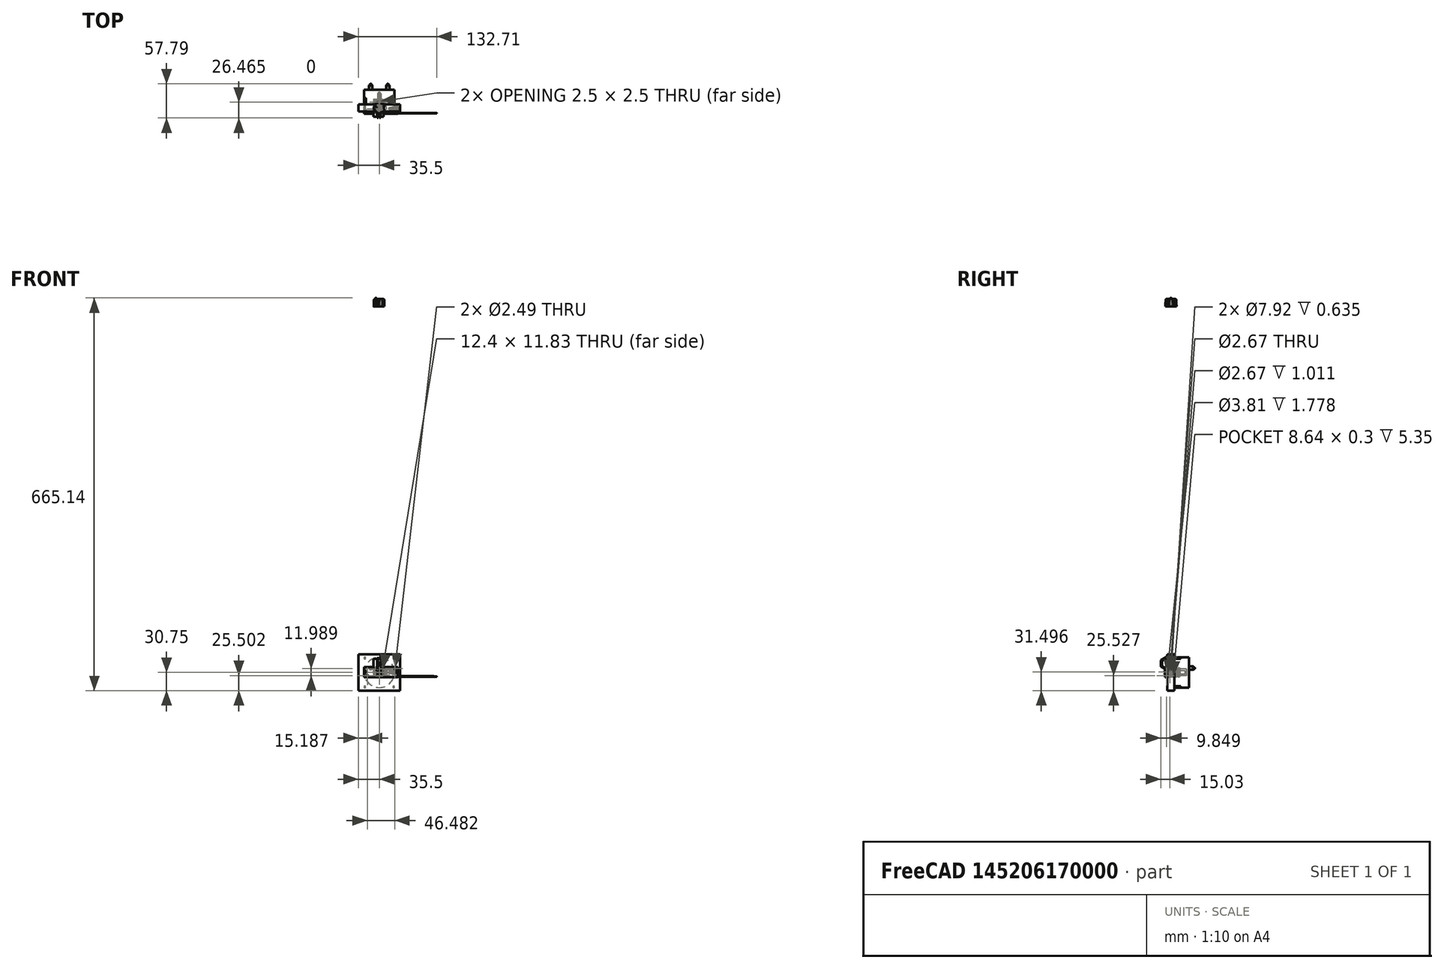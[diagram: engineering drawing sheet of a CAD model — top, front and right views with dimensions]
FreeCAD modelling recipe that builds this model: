
FCSTD DOCUMENT  (FreeCAD 1.0R39109 (Git))
Label: console-placement
License: All rights reserved
LicenseURL: https://en.wikipedia.org/wiki/All_rights_reserved
objects: App::Link×22, Part::Feature×7, App::FeaturePython×6, App::Part×3, Sketcher::SketchObject×3, PartDesign::Pad×3, Assembly::AssemblyLink×1, PartDesign::Plane×1, PartDesign::Body×1, Assembly::JointGroup×1, Assembly::AssemblyObject×1
note: 24 computed .brp shape members not serialized (recipe doc carries the construction recipe); baked Part::Feature solids carry a one-line shape summary decoded from their .brp
EXTERNAL_REF file=PCB.FCStd obj=Assembly
EXTERNAL_REF file=PCB.FCStd obj=pcb_imported
EXTERNAL_REF file=PCB.FCStd obj=WP154A4SUREQBFZGC
EXTERNAL_REF file=PCB.FCStd obj=WP154A4SUREQBFZGC001
EXTERNAL_REF file=PCB.FCStd obj=WP154A4SUREQBFZGC002
EXTERNAL_REF file=PCB.FCStd obj=WP154A4SUREQBFZGC003
EXTERNAL_REF file=PCB.FCStd obj=WP154A4SUREQBFZGC004
EXTERNAL_REF file=PCB.FCStd obj=WP154A4SUREQBFZGC005
EXTERNAL_REF file=PCB.FCStd obj=Dual_RCA
EXTERNAL_REF file=PCB.FCStd obj=Pro_Mini
EXTERNAL_REF file=PCB.FCStd obj=SPST_momentary001
EXTERNAL_REF file=PCB.FCStd obj=_pinconnector_640441_3
EXTERNAL_REF file=PCB.FCStd obj=_pinconnector_640441_004
EXTERNAL_REF file=PCB.FCStd obj=_pinconnector_640441_005
EXTERNAL_REF file=PCB.FCStd obj=CUI_PJ_202A
EXTERNAL_REF file=PCB.FCStd obj=SLW_864547_5A_RA_D
EXTERNAL_REF file=PCB.FCStd obj=SLW_864547_5A_RA_D001
EXTERNAL_REF file=PCB.FCStd obj=Ft232H_2_assembly001

FEATURE [App::Link] pcb_imported  label="pcb imported001"
  LinkedObject = -> <external PCB.FCStd>#pcb_imported
FEATURE [App::Link] WP154A4SUREQBFZGC  label="WP154A4SUREQBFZGC001"
  LinkPlacement = pos=(54.356,15.113,4.572) rot=(0,1,0;1.5708rad)
  LinkedObject = -> <external PCB.FCStd>#WP154A4SUREQBFZGC
  Placement = pos=(54.356,15.113,4.572) rot=(0,1,0;1.5708rad)
FEATURE [App::Link] WP154A4SUREQBFZGC001  label="WP154A4SUREQBFZGC002"
  LinkPlacement = pos=(54.356,28.448,4.572) rot=(0,1,0;1.5708rad)
  LinkedObject = -> <external PCB.FCStd>#WP154A4SUREQBFZGC001
  Placement = pos=(54.356,28.448,4.572) rot=(0,1,0;1.5708rad)
FEATURE [App::Link] WP154A4SUREQBFZGC002  label="WP154A4SUREQBFZGC003"
  LinkPlacement = pos=(54.356,50.038,4.572) rot=(0,1,0;1.5708rad)
  LinkedObject = -> <external PCB.FCStd>#WP154A4SUREQBFZGC002
  Placement = pos=(54.356,50.038,4.572) rot=(0,1,0;1.5708rad)
FEATURE [App::Link] WP154A4SUREQBFZGC003  label="WP154A4SUREQBFZGC004"
  LinkPlacement = pos=(54.356,63.373,4.572) rot=(0,1,0;1.5708rad)
  LinkedObject = -> <external PCB.FCStd>#WP154A4SUREQBFZGC003
  Placement = pos=(54.356,63.373,4.572) rot=(0,1,0;1.5708rad)
FEATURE [App::Link] WP154A4SUREQBFZGC004  label="WP154A4SUREQBFZGC005"
  LinkPlacement = pos=(54.356,84.963,4.572) rot=(0,1,0;1.5708rad)
  LinkedObject = -> <external PCB.FCStd>#WP154A4SUREQBFZGC004
  Placement = pos=(54.356,84.963,4.572) rot=(0,1,0;1.5708rad)
FEATURE [App::Link] WP154A4SUREQBFZGC005  label="WP154A4SUREQBFZGC006"
  LinkPlacement = pos=(54.356,98.298,4.572) rot=(0,1,0;1.5708rad)
  LinkedObject = -> <external PCB.FCStd>#WP154A4SUREQBFZGC005
  Placement = pos=(54.356,98.298,4.572) rot=(0,1,0;1.5708rad)
FEATURE [App::Link] Dual_RCA  label="Dual RCA001"
  LinkPlacement = pos=(0.032625,91.9586,15.028) rot=(0,0,-1;1.5708rad)
  LinkedObject = -> <external PCB.FCStd>#Dual_RCA
  Placement = pos=(0.032625,91.9586,15.028) rot=(0,0,-1;1.5708rad)
FEATURE [App::Link] Pro_Mini  label="Pro Mini001"
  LinkPlacement = pos=(28.575,39.37,11.938) rot=(0,0,1;4.71239rad)
  LinkedObject = -> <external PCB.FCStd>#Pro_Mini
  Placement = pos=(28.575,39.37,11.938) rot=(0,0,1;4.71239rad)
FEATURE [App::Link] SPST_momentary001  label="SPST-momentary001"
  LinkPlacement = pos=(9.02102,11.6417,1.678) rot=(-0.57735,0.57735,0.57735;4.18879rad)
  LinkedObject = -> <external PCB.FCStd>#SPST_momentary001
  Placement = pos=(9.02102,11.6417,1.678) rot=(-0.57735,0.57735,0.57735;4.18879rad)
FEATURE [App::Link] _pinconnector_640441_3  label="3pinconnector-640441-004"
  LinkPlacement = pos=(45.7412,2.54,1.778) rot=(0,1,0;3.14159rad)
  LinkedObject = -> <external PCB.FCStd>#_pinconnector_640441_3
  Placement = pos=(45.7412,2.54,1.778) rot=(0,1,0;3.14159rad)
FEATURE [App::Link] _pinconnector_640441_004  label="3pinconnector-640441-005"
  LinkPlacement = pos=(4.445,29.845,1.778) rot=(0,1,0;3.14159rad)
  LinkedObject = -> <external PCB.FCStd>#_pinconnector_640441_004
  Placement = pos=(4.445,29.845,1.778) rot=(0,1,0;3.14159rad)
FEATURE [App::Link] _pinconnector_640441_005  label="3pinconnector-640441-006"
  LinkPlacement = pos=(33.0962,92.7862,1.778) rot=(0,1,0;3.14159rad)
  LinkedObject = -> <external PCB.FCStd>#_pinconnector_640441_005
  Placement = pos=(33.0962,92.7862,1.778) rot=(0,1,0;3.14159rad)
FEATURE [App::Link] CUI_PJ_202A  label="CUI_PJ-202A001"
  LinkPlacement = pos=(-2.69501,66.04,8.278) rot=(0,0.707107,0.707107;3.14159rad)
  LinkedObject = -> <external PCB.FCStd>#CUI_PJ_202A
  Placement = pos=(-2.69501,66.04,8.278) rot=(0,0.707107,0.707107;3.14159rad)
FEATURE [App::Link] SLW_864547_5A_RA_D  label="SLW-864547-5A-RA-D001"
  LinkPlacement = pos=(2.563,37.056,1.72323) rot=(0,0,1;4.71239rad)
  LinkedObject = -> <external PCB.FCStd>#SLW_864547_5A_RA_D
  Placement = pos=(2.563,37.056,1.72323) rot=(0,0,1;4.71239rad)
FEATURE [App::Link] SLW_864547_5A_RA_D001  label="SLW-864547-5A-RA-D002"
  LinkPlacement = pos=(2.563,49.756,1.72323) rot=(0,0,1;4.71239rad)
  LinkedObject = -> <external PCB.FCStd>#SLW_864547_5A_RA_D001
  Placement = pos=(2.563,49.756,1.72323) rot=(0,0,1;4.71239rad)
FEATURE [App::Link] Ft232H_2_assembly001  label="Ft232H-2-assembly001"
  LinkPlacement = pos=(37.8726,15.185,11.684) rot=(1,0,0;1.5708rad)
  LinkedObject = -> <external PCB.FCStd>#Ft232H_2_assembly001
  Placement = pos=(37.8726,15.185,11.684) rot=(1,0,0;1.5708rad)
FEATURE [Assembly::AssemblyLink] PCB_Assembly  label="PCB Assembly"
  Group = -> [pcb_imported,WP154A4SUREQBFZGC,WP154A4SUREQBFZGC001,WP154A4SUREQBFZGC002,WP154A4SUREQBFZGC003,WP154A4SUREQBFZGC004,WP154A4SUREQBFZGC005,Dual_RCA,Pro_Mini,SPST_momentary001,_pinconnector_640441_3,_pinconnector_640441_004,_pinconnector_640441_005,CUI_PJ_202A,SLW_864547_5A_RA_D,SLW_864547_5A_RA_D001,Ft232H_2_assembly001]
  LinkedObject = -> <external PCB.FCStd>#Assembly
  Origin = -> Origin001
  Rigid = true
FEATURE [App::FeaturePython] GroundedJoint  # Assembly grounded joint (typed FeaturePython)
  ObjectToGround = -> PCB_Assembly
FEATURE [Part::Feature] Part__Feature  label="meter"
  shape: bbox 71 x 47.12 x 61.5 mm, 22 faces (baked)
FEATURE [App::Link] meter  label="meter001"
  LinkPlacement = pos=(82.55,12.7,55.88) rot=(0,0,1;1.5708rad)
  LinkedObject = -> Part__Feature
  Placement = pos=(82.55,12.7,55.88) rot=(0,0,1;1.5708rad)
FEATURE [App::FeaturePython] Joint  label="meter 1"  # Assembly joint (typed FeaturePython)
  Activated = true
  AngleMax = 0
  AngleMin = 0
  Detach1 = false
  Detach2 = false
  Distance = 0
  Distance2 = 0
  EnableAngleMax = false
  EnableAngleMin = false
  EnableLengthMax = false
  EnableLengthMin = false
  JointType = 0 (Fixed)
  LengthMax = 0
  LengthMin = 0
  Offset1 = pos=(-12.7,82.55,-55.88) rot=(0,0,-1;1.5708rad)
  Placement1 = pos=(-12.7,82.55,-55.88) rot=(0,0,-1;1.5708rad)
  Reference1 = -> Assembly [meter.,meter.]
  Reference2 = -> Assembly [PCB_Assembly.,PCB_Assembly.]
FEATURE [App::Link] meter001  label="meter002"
  LinkPlacement = pos=(82.55,101.6,55.88) rot=(0,0,1;1.5708rad)
  LinkedObject = -> Part__Feature
  Placement = pos=(82.55,101.6,55.88) rot=(0,0,1;1.5708rad)
FEATURE [App::FeaturePython] Joint001  label="meter 2 wrt 1"  # Assembly joint (typed FeaturePython)
  Activated = true
  AngleMax = 0
  AngleMin = 0
  Detach1 = false
  Detach2 = false
  Distance = 0
  Distance2 = 0
  EnableAngleMax = false
  EnableAngleMin = false
  EnableLengthMax = false
  EnableLengthMin = false
  JointType = 0 (Fixed)
  LengthMax = 0
  LengthMin = 0
  Offset1 = pos=(-88.9,0,0) rot=(0,0,1;0rad)
  Placement1 = pos=(-88.9,0,0) rot=(0,0,1;0rad)
  Reference1 = -> Assembly [meter001.,meter001.]
  Reference2 = -> Assembly [meter.,meter.]
FEATURE [Part::Feature] Part__Feature001  label="1M-pot"
  shape: bbox 24.75 x 24.5 x 16.5 mm, 34 faces (baked)
FEATURE [App::Link] _M_pot  label="1M-pot001"
  LinkPlacement = pos=(79.0499,-6.858,7.62) rot=(0.707107,0.707107,0;3.14159rad)
  LinkedObject = -> Part__Feature001
  Placement = pos=(79.0499,-6.858,7.62) rot=(0.707107,0.707107,0;3.14159rad)
FEATURE [App::FeaturePython] Joint002  label="pot joint"  # Assembly joint (typed FeaturePython)
  Activated = true
  AngleMax = 0
  AngleMin = 0
  Detach1 = false
  Detach2 = false
  Distance = 0
  Distance2 = 0
  EnableAngleMax = false
  EnableAngleMin = false
  EnableLengthMax = false
  EnableLengthMin = false
  JointType = 0 (Fixed)
  LengthMax = 0
  LengthMin = 0
  Offset1 = pos=(6.858,-79.0499,7.62) rot=(0,0,1;1.5708rad)
  Placement1 = pos=(6.858,-79.0499,7.62) rot=(0,0,1;1.5708rad)
  Reference1 = -> Assembly [_M_pot.,_M_pot.]
  Reference2 = -> Assembly [PCB_Assembly.,PCB_Assembly.]
FEATURE [Part::Feature] Part__Feature002  label="300DP6R7BLKM3QEBLK"
  shape: bbox 17.98 x 22.36 x 12.23 mm, 297 faces (baked)
FEATURE [Part::Feature] Part__Feature003  label="300DP6R7BLKM3QEBLK001"
  shape: bbox 19.85 x 2.3 x 15.8 mm, 12 faces (baked)
FEATURE [Part::Feature] Part__Feature004  label="300DP6R7BLKM3QEBLK002"
  shape: bbox 15.43 x 20.8 x 13 mm, 50 faces (baked)
FEATURE [App::Part] _00DP6R7BLKM3QEBLK  label="300DP6R7BLKM3QEBLK003"
  Group = -> [Part__Feature002,Part__Feature003,Part__Feature004]
  Origin = -> Origin002
FEATURE [App::Link] _00DP6R7BLKM3QEBLK003  label="300DP6R7BLKM3QEBLK004"
  LinkPlacement = pos=(77.7748,127,7.62) rot=(0.57735,0.57735,-0.57735;2.0944rad)
  LinkedObject = -> _00DP6R7BLKM3QEBLK
  Placement = pos=(77.7748,127,7.62) rot=(0.57735,0.57735,-0.57735;2.0944rad)
FEATURE [App::FeaturePython] Joint003  label="SP3T joint"  # Assembly joint (typed FeaturePython)
  Activated = true
  AngleMax = 0
  AngleMin = 0
  Detach1 = false
  Detach2 = false
  Distance = 0
  Distance2 = 0
  EnableAngleMax = false
  EnableAngleMin = false
  EnableLengthMax = false
  EnableLengthMin = false
  JointType = 0 (Fixed)
  LengthMax = 0
  LengthMin = 0
  Offset1 = pos=(7.62,-77.7748,127) rot=(0.57735,0.57735,0.57735;2.0944rad)
  Placement1 = pos=(7.62,-77.7748,127) rot=(0.57735,0.57735,0.57735;2.0944rad)
  Reference1 = -> Assembly [_00DP6R7BLKM3QEBLK003.,_00DP6R7BLKM3QEBLK003.]
  Reference2 = -> Assembly [PCB_Assembly.,PCB_Assembly.]
FEATURE [Sketcher::SketchObject] Sketch
  ArcFitTolerance = 1e-06
  AttachmentSupport = -> [XY_Plane004]
  FullyConstrained = true
  MakeInternals = false
  MapMode = 5
  sketch-geometry (1):
    g0: Circle CenterX=0 CenterY=0 CenterZ=0 NormalX=0 NormalY=0 NormalZ=1 AngleXU=0 Radius=9.15
  constraints (2):
    c: Coincident(g0,g-1)
    c: Diameter(g0) = 18.3
FEATURE [PartDesign::Pad] Pad
  Direction = (0,0,1)
  Length = 2
  Length2 = 10
  Profile = -> Sketch
  ReferenceAxis = -> Sketch [N_Axis]
  Refine = true
  Suppressed = false
  Type = 0
FEATURE [Sketcher::SketchObject] Sketch001
  ArcFitTolerance = 1e-06
  AttachmentSupport = -> [XY_Plane004]
  FullyConstrained = true
  MakeInternals = false
  MapMode = 5
  sketch-geometry (1):
    g0: Circle CenterX=0 CenterY=0 CenterZ=0 NormalX=0 NormalY=0 NormalZ=1 AngleXU=0 Radius=7.75
  constraints (2):
    c: Diameter(g0) = 15.5
    c: Coincident(g0,g-1)
FEATURE [PartDesign::Pad] Pad001
  BaseFeature = -> Pad
  Direction = (0,0,1)
  Length = 17
  Length2 = 10
  Midplane = true
  Profile = -> Sketch001
  ReferenceAxis = -> Sketch001 [N_Axis]
  Refine = true
  Suppressed = false
  Type = 0
FEATURE [PartDesign::Plane] DatumPlane
  AttachmentOffset = pos=(0,0,-2) rot=(0,0,1;0rad)
  AttachmentSupport = -> [XY_Plane004]
  Length = 60.0456
  MapMode = 5
  Placement = pos=(0,0,-2) rot=(0,0,1;0rad)
  ResizeMode = 0
  Width = 60.0456
FEATURE [Sketcher::SketchObject] Sketch002
  ArcFitTolerance = 1e-06
  AttachmentSupport = -> [DatumPlane]
  FullyConstrained = true
  MakeInternals = false
  MapMode = 5
  Placement = pos=(0,0,-2) rot=(0,0,1;0rad)
  sketch-geometry (7):
    g0: LineSegment StartX=-5.48483 StartY=9.5 StartZ=0 EndX=-10.9697 EndY=0 EndZ=0
    g1: LineSegment StartX=-10.9697 StartY=0 StartZ=0 EndX=-5.48483 EndY=-9.5 EndZ=0
    g2: LineSegment StartX=-5.48483 StartY=-9.5 StartZ=0 EndX=5.48483 EndY=-9.5 EndZ=0
    g3: LineSegment StartX=5.48483 StartY=-9.5 StartZ=0 EndX=10.9697 EndY=1.8e-15 EndZ=0
    g4: LineSegment StartX=10.9697 StartY=1.8e-15 StartZ=0 EndX=5.48483 EndY=9.5 EndZ=0
    g5: LineSegment StartX=5.48483 StartY=9.5 StartZ=0 EndX=-5.48483 EndY=9.5 EndZ=0
    g6: Circle [constr] CenterX=0 CenterY=0 CenterZ=0 NormalX=0 NormalY=0 NormalZ=1 AngleXU=0 Radius=10.9697
  constraints (16):
    c: Coincident(g0,g1)
    c: Coincident(g1,g2)
    c: Coincident(g2,g3)
    c: Coincident(g3,g4)
    c: Coincident(g4,g5)
    c: Coincident(g5,g0)
    c: Equal(g0, g1-g5) x5
    c: PointOnObject(g0,g6)
    c: PointOnObject(g1,g6)
    c: PointOnObject(g2,g6)
    c: PointOnObject(g3,g6)
    c: PointOnObject(g4,g6)
    c: PointOnObject(g5,g6)
    c: Coincident(g6,g-1)
    c: Horizontal(g5)
    c: DistanceY(g2,g4) = 19
FEATURE [PartDesign::Pad] Pad002
  BaseFeature = -> Pad001
  Direction = (0,0,1)
  Length = 2
  Length2 = 10
  Profile = -> Sketch002
  ReferenceAxis = -> Sketch002 [N_Axis]
  Refine = true
  Reversed = true
  Suppressed = false
  Type = 0
FEATURE [PartDesign::Body] Body
  AllowCompound = false
  Group = -> [Sketch,Pad,Sketch001,Pad001,DatumPlane,Sketch002,Pad002]
  Origin = -> Origin004
  Placement = pos=(-1.524,-7.62,15.24) rot=(0,1,0;4.71239rad)
  Tip = -> Pad002
FEATURE [App::Part] Part  label="Cliff FC684204"
  Group = -> [Body]
  Origin = -> Origin003
FEATURE [Part::Feature] Part__Feature005  label="AA single"
  shape: bbox 122.8 x 13.91 x 16.91 mm, 627 faces (baked)
FEATURE [App::Part] AA_single  label="AA single002"
  Group = -> [Part__Feature005]
  Origin = -> Origin005
FEATURE [Part::Feature] Part__Feature006  label="knob"
  shape: bbox 18.73 x 19.3 x 14.61 mm, 41 faces (baked)
FEATURE [App::Link] knob  label="knob001"
  LinkPlacement = pos=(-525.356,-6.858,7.62) rot=(0,1,0;1.5708rad)
  LinkedObject = -> Part__Feature006
  Placement = pos=(-525.356,-6.858,7.62) rot=(0,1,0;1.5708rad)
FEATURE [App::FeaturePython] Joint006  label="Revolute"  # Assembly joint (typed FeaturePython)
  Activated = true
  AngleMax = 0
  AngleMin = 0
  Detach1 = false
  Detach2 = false
  Distance = 0
  Distance2 = 0
  EnableAngleMax = false
  EnableAngleMin = false
  EnableLengthMax = false
  EnableLengthMin = false
  JointType = 1 (Revolute)
  LengthMax = 0
  LengthMin = 0
  Offset1 = pos=(0,0,203.2) rot=(0,0,1;0rad)
  Placement1 = pos=(-1.31779e-06,0,628.906) rot=(0,-1,0;3.14159rad)
  Placement2 = pos=(0,24.5,9e-16) rot=(-0.57735,-0.57735,0.57735;4.18879rad)
  Reference1 = -> Assembly [knob.Face2,knob.Face2]
  Reference2 = -> Assembly [_M_pot.Face6,_M_pot.Edge1]
FEATURE [Assembly::JointGroup] Joints
  Group = -> [GroundedJoint,Joint,Joint001,Joint002,Joint003,Joint006]
FEATURE [Assembly::AssemblyObject] Assembly
  Group = -> [Joints,PCB_Assembly,GroundedJoint,meter,Joint,meter001,Joint001,_M_pot,Joint002,_00DP6R7BLKM3QEBLK003,Joint003,knob,Joint006]
  Origin = -> Origin
  Type = Assembly

RESOLVED EXTERNAL PARTS (link-assembly join: the EXTERNAL_REF files above that resolve inside this repo's crawl, each included once):
---- part PCB.FCStd = doc fcstd_af2e7ee1fe31 ----
FCSTD DOCUMENT  (FreeCAD 1.0R39109 (Git))
Label: PCB
License: All rights reserved
LicenseURL: https://en.wikipedia.org/wiki/All_rights_reserved
objects: App::Link×17, App::FeaturePython×17, Part::Feature×15, Sketcher::SketchObject×3, App::Part×3, PartDesign::Pad×2, PartDesign::Body×2, PartDesign::Pocket×1, Assembly::JointGroup×1, Assembly::AssemblyObject×1, PartDesign::SubShapeBinder×1
note: 33 computed .brp shape members not serialized (recipe doc carries the construction recipe); baked Part::Feature solids carry a one-line shape summary decoded from their .brp

FEATURE [Sketcher::SketchObject] MainSketch
  ArcFitTolerance = 1e-06
  AttachmentSupport = -> [XY_Plane]
  FullyConstrained = false
  MakeInternals = false
  MapMode = 5
  sketch-geometry (4):
    g0: LineSegment StartX=0 StartY=0 StartZ=0 EndX=50.8 EndY=0 EndZ=0
    g1: LineSegment StartX=50.8 StartY=0 StartZ=0 EndX=50.8 EndY=101.6 EndZ=0
    g2: LineSegment StartX=50.8 StartY=101.6 StartZ=0 EndX=0 EndY=101.6 EndZ=0
    g3: LineSegment StartX=0 StartY=101.6 StartZ=0 EndX=0 EndY=0 EndZ=0
  constraints (4):
    c: Horizontal(g0)
    c: Horizontal(g2)
    c: Vertical(g1)
    c: Vertical(g3)
FEATURE [PartDesign::Pad] Main
  Direction = (0,0,1)
  Length = 1.778
  Length2 = 100.076
  Profile = -> MainSketch
  Refine = true
  Suppressed = false
  Type = 0
FEATURE [Sketcher::SketchObject] HoleSketch
  ArcFitTolerance = 1e-06
  AttachmentSupport = -> [XY_Plane]
  FullyConstrained = false
  MakeInternals = false
  MapMode = 5
  sketch-geometry (197):
    g0: Circle CenterX=41.275 CenterY=47.117 CenterZ=0 NormalX=0 NormalY=0 NormalZ=1 AngleXU=0 Radius=0.508
    g1: Circle CenterX=38.735 CenterY=47.117 CenterZ=0 NormalX=0 NormalY=0 NormalZ=1 AngleXU=0 Radius=0.508
    g2: Circle CenterX=36.195 CenterY=47.117 CenterZ=0 NormalX=0 NormalY=0 NormalZ=1 AngleXU=0 Radius=0.508
    g3: Circle CenterX=13.335 CenterY=47.117 CenterZ=0 NormalX=0 NormalY=0 NormalZ=1 AngleXU=0 Radius=0.508
    g4: Circle CenterX=33.655 CenterY=47.117 CenterZ=0 NormalX=0 NormalY=0 NormalZ=1 AngleXU=0 Radius=0.508
    g5: Circle CenterX=15.875 CenterY=47.117 CenterZ=0 NormalX=0 NormalY=0 NormalZ=1 AngleXU=0 Radius=0.508
    g6: Circle CenterX=31.115 CenterY=47.117 CenterZ=0 NormalX=0 NormalY=0 NormalZ=1 AngleXU=0 Radius=0.508
    g7: Circle CenterX=28.575 CenterY=47.117 CenterZ=0 NormalX=0 NormalY=0 NormalZ=1 AngleXU=0 Radius=0.508
    g8: Circle CenterX=26.035 CenterY=47.117 CenterZ=0 NormalX=0 NormalY=0 NormalZ=1 AngleXU=0 Radius=0.508
    g9: Circle CenterX=18.415 CenterY=47.117 CenterZ=0 NormalX=0 NormalY=0 NormalZ=1 AngleXU=0 Radius=0.508
    g10: Circle CenterX=20.955 CenterY=47.117 CenterZ=0 NormalX=0 NormalY=0 NormalZ=1 AngleXU=0 Radius=0.508
    g11: Circle CenterX=23.495 CenterY=47.117 CenterZ=0 NormalX=0 NormalY=0 NormalZ=1 AngleXU=0 Radius=0.508
    g12: Circle CenterX=15.875 CenterY=31.877 CenterZ=0 NormalX=0 NormalY=0 NormalZ=1 AngleXU=0 Radius=0.508
    g13: Circle CenterX=13.335 CenterY=31.877 CenterZ=0 NormalX=0 NormalY=0 NormalZ=1 AngleXU=0 Radius=0.508
    g14: Circle CenterX=20.955 CenterY=31.877 CenterZ=0 NormalX=0 NormalY=0 NormalZ=1 AngleXU=0 Radius=0.508
    g15: Circle CenterX=18.415 CenterY=31.877 CenterZ=0 NormalX=0 NormalY=0 NormalZ=1 AngleXU=0 Radius=0.508
    g16: Circle CenterX=26.035 CenterY=31.877 CenterZ=0 NormalX=0 NormalY=0 NormalZ=1 AngleXU=0 Radius=0.508
    g17: Circle CenterX=23.495 CenterY=31.877 CenterZ=0 NormalX=0 NormalY=0 NormalZ=1 AngleXU=0 Radius=0.508
    g18: Circle CenterX=31.115 CenterY=31.877 CenterZ=0 NormalX=0 NormalY=0 NormalZ=1 AngleXU=0 Radius=0.508
    g19: Circle CenterX=28.575 CenterY=31.877 CenterZ=0 NormalX=0 NormalY=0 NormalZ=1 AngleXU=0 Radius=0.508
    g20: Circle CenterX=36.195 CenterY=31.877 CenterZ=0 NormalX=0 NormalY=0 NormalZ=1 AngleXU=0 Radius=0.508
    g21: Circle CenterX=33.655 CenterY=31.877 CenterZ=0 NormalX=0 NormalY=0 NormalZ=1 AngleXU=0 Radius=0.508
    g22: Circle CenterX=41.275 CenterY=31.877 CenterZ=0 NormalX=0 NormalY=0 NormalZ=1 AngleXU=0 Radius=0.508
    g23: Circle CenterX=38.735 CenterY=31.877 CenterZ=0 NormalX=0 NormalY=0 NormalZ=1 AngleXU=0 Radius=0.508
    g24: Circle CenterX=22.225 CenterY=34.925 CenterZ=0 NormalX=0 NormalY=0 NormalZ=1 AngleXU=0 Radius=0.508
    g25: Circle CenterX=19.685 CenterY=34.925 CenterZ=0 NormalX=0 NormalY=0 NormalZ=1 AngleXU=0 Radius=0.508
    g26: Circle CenterX=32.385 CenterY=34.925 CenterZ=0 NormalX=0 NormalY=0 NormalZ=1 AngleXU=0 Radius=0.508
    g27: Circle CenterX=29.845 CenterY=34.925 CenterZ=0 NormalX=0 NormalY=0 NormalZ=1 AngleXU=0 Radius=0.508
    g28: Circle CenterX=43.815 CenterY=43.307 CenterZ=0 NormalX=0 NormalY=0 NormalZ=1 AngleXU=0 Radius=0.508
    g29: Circle CenterX=43.815 CenterY=40.767 CenterZ=0 NormalX=0 NormalY=0 NormalZ=1 AngleXU=0 Radius=0.508
    g30: Circle CenterX=43.815 CenterY=38.227 CenterZ=0 NormalX=0 NormalY=0 NormalZ=1 AngleXU=0 Radius=0.508
    g31: Circle CenterX=43.815 CenterY=35.687 CenterZ=0 NormalX=0 NormalY=0 NormalZ=1 AngleXU=0 Radius=0.508
    g32: Circle CenterX=43.815 CenterY=33.147 CenterZ=0 NormalX=0 NormalY=0 NormalZ=1 AngleXU=0 Radius=0.508
    g33: Circle CenterX=16.51 CenterY=25.4 CenterZ=0 NormalX=0 NormalY=0 NormalZ=1 AngleXU=0 Radius=0.508
    g34: Circle CenterX=8.89 CenterY=5.08 CenterZ=0 NormalX=0 NormalY=0 NormalZ=1 AngleXU=0 Radius=0.508
    g35: Circle CenterX=19.05 CenterY=25.4 CenterZ=0 NormalX=0 NormalY=0 NormalZ=1 AngleXU=0 Radius=0.508
    g36: Circle CenterX=11.43 CenterY=5.08 CenterZ=0 NormalX=0 NormalY=0 NormalZ=1 AngleXU=0 Radius=0.508
    g37: Circle CenterX=13.97 CenterY=5.08 CenterZ=0 NormalX=0 NormalY=0 NormalZ=1 AngleXU=0 Radius=0.508
    g38: Circle CenterX=16.51 CenterY=5.08 CenterZ=0 NormalX=0 NormalY=0 NormalZ=1 AngleXU=0 Radius=0.508
    g39: Circle CenterX=19.05 CenterY=5.08 CenterZ=0 NormalX=0 NormalY=0 NormalZ=1 AngleXU=0 Radius=0.508
    g40: Circle CenterX=21.59 CenterY=5.08 CenterZ=0 NormalX=0 NormalY=0 NormalZ=1 AngleXU=0 Radius=0.508
    g41: Circle CenterX=24.13 CenterY=5.08 CenterZ=0 NormalX=0 NormalY=0 NormalZ=1 AngleXU=0 Radius=0.508
    g42: Circle CenterX=26.67 CenterY=5.08 CenterZ=0 NormalX=0 NormalY=0 NormalZ=1 AngleXU=0 Radius=0.508
    g43: Circle CenterX=29.21 CenterY=25.4 CenterZ=0 NormalX=0 NormalY=0 NormalZ=1 AngleXU=0 Radius=0.508
    g44: Circle CenterX=29.21 CenterY=5.08 CenterZ=0 NormalX=0 NormalY=0 NormalZ=1 AngleXU=0 Radius=0.508
    g45: Circle CenterX=31.75 CenterY=25.4 CenterZ=0 NormalX=0 NormalY=0 NormalZ=1 AngleXU=0 Radius=0.508
    g46: Circle CenterX=31.75 CenterY=5.08 CenterZ=0 NormalX=0 NormalY=0 NormalZ=1 AngleXU=0 Radius=0.508
    g47: Circle CenterX=11.5358 CenterY=9.05933 CenterZ=0 NormalX=0 NormalY=0 NormalZ=1 AngleXU=0 Radius=0.508
    g48: Circle CenterX=11.5358 CenterY=14.1393 CenterZ=0 NormalX=0 NormalY=0 NormalZ=1 AngleXU=0 Radius=0.508
    g49: Circle CenterX=6.45583 CenterY=9.05933 CenterZ=0 NormalX=0 NormalY=0 NormalZ=1 AngleXU=0 Radius=0.508
    g50: Circle CenterX=6.45583 CenterY=14.1393 CenterZ=0 NormalX=0 NormalY=0 NormalZ=1 AngleXU=0 Radius=0.508
    g51: Circle CenterX=6.985 CenterY=29.845 CenterZ=0 NormalX=0 NormalY=0 NormalZ=1 AngleXU=0 Radius=0.508
    g52: Circle CenterX=4.445 CenterY=29.845 CenterZ=0 NormalX=0 NormalY=0 NormalZ=1 AngleXU=0 Radius=0.508
    g53: Circle CenterX=1.905 CenterY=29.845 CenterZ=0 NormalX=0 NormalY=0 NormalZ=1 AngleXU=0 Radius=0.508
    g54: Circle CenterX=44.45 CenterY=25.781 CenterZ=0 NormalX=0 NormalY=0 NormalZ=1 AngleXU=0 Radius=0.508
    g55: Circle CenterX=44.45 CenterY=23.241 CenterZ=0 NormalX=0 NormalY=0 NormalZ=1 AngleXU=0 Radius=0.508
    g56: Circle CenterX=44.45 CenterY=20.701 CenterZ=0 NormalX=0 NormalY=0 NormalZ=1 AngleXU=0 Radius=0.508
    g57: Circle CenterX=41.91 CenterY=25.781 CenterZ=0 NormalX=0 NormalY=0 NormalZ=1 AngleXU=0 Radius=0.508
    g58: Circle CenterX=41.91 CenterY=23.241 CenterZ=0 NormalX=0 NormalY=0 NormalZ=1 AngleXU=0 Radius=0.508
    g59: Circle CenterX=41.91 CenterY=20.701 CenterZ=0 NormalX=0 NormalY=0 NormalZ=1 AngleXU=0 Radius=0.508
    g60: Circle CenterX=43.18 CenterY=2.54 CenterZ=0 NormalX=0 NormalY=0 NormalZ=1 AngleXU=0 Radius=0.508
    g61: Circle CenterX=45.72 CenterY=2.54 CenterZ=0 NormalX=0 NormalY=0 NormalZ=1 AngleXU=0 Radius=0.508
    g62: Circle CenterX=48.26 CenterY=2.54 CenterZ=0 NormalX=0 NormalY=0 NormalZ=1 AngleXU=0 Radius=0.508
    g63: Circle CenterX=28.575 CenterY=99.06 CenterZ=0 NormalX=0 NormalY=0 NormalZ=1 AngleXU=0 Radius=0.508
    g64: Circle CenterX=31.115 CenterY=99.06 CenterZ=0 NormalX=0 NormalY=0 NormalZ=1 AngleXU=0 Radius=0.508
    g65: Circle CenterX=38.735 CenterY=99.06 CenterZ=0 NormalX=0 NormalY=0 NormalZ=1 AngleXU=0 Radius=0.508
    g66: Circle CenterX=36.195 CenterY=99.06 CenterZ=0 NormalX=0 NormalY=0 NormalZ=1 AngleXU=0 Radius=0.508
    g67: Circle CenterX=10.16 CenterY=54.61 CenterZ=0 NormalX=0 NormalY=0 NormalZ=1 AngleXU=0 Radius=0.508
    g68: Circle CenterX=12.7 CenterY=54.61 CenterZ=0 NormalX=0 NormalY=0 NormalZ=1 AngleXU=0 Radius=0.508
    g69: Circle CenterX=13.335 CenterY=97.155 CenterZ=0 NormalX=0 NormalY=0 NormalZ=1 AngleXU=0 Radius=0.254
    g70: Circle CenterX=46.5032 CenterY=71.3317 CenterZ=0 NormalX=0 NormalY=0 NormalZ=1 AngleXU=0 Radius=0.254
    g71: Circle CenterX=30.48 CenterY=92.71 CenterZ=0 NormalX=0 NormalY=0 NormalZ=1 AngleXU=0 Radius=0.508
    g72: Circle CenterX=33.02 CenterY=92.71 CenterZ=0 NormalX=0 NormalY=0 NormalZ=1 AngleXU=0 Radius=0.508
    g73: Circle CenterX=35.56 CenterY=92.71 CenterZ=0 NormalX=0 NormalY=0 NormalZ=1 AngleXU=0 Radius=0.508
    g74: Circle CenterX=45.085 CenterY=66.8867 CenterZ=0 NormalX=0 NormalY=0 NormalZ=1 AngleXU=0 Radius=0.254
    g75: Circle CenterX=25.8445 CenterY=41.91 CenterZ=0 NormalX=0 NormalY=0 NormalZ=1 AngleXU=0 Radius=0.254
    g76: Circle CenterX=44.9157 CenterY=70.4003 CenterZ=0 NormalX=0 NormalY=0 NormalZ=1 AngleXU=0 Radius=0.254
    g77: Circle CenterX=41.6348 CenterY=69.4055 CenterZ=0 NormalX=0 NormalY=0 NormalZ=1 AngleXU=0 Radius=0.254
    g78: Circle CenterX=33.655 CenterY=56.515 CenterZ=0 NormalX=0 NormalY=0 NormalZ=1 AngleXU=0 Radius=0.254
    g79: Circle CenterX=34.925 CenterY=53.8903 CenterZ=0 NormalX=0 NormalY=0 NormalZ=1 AngleXU=0 Radius=0.254
    g80: Circle CenterX=17.78 CenterY=84.074 CenterZ=0 NormalX=0 NormalY=0 NormalZ=1 AngleXU=0 Radius=0.254
    g81: Circle CenterX=38.735 CenterY=43.18 CenterZ=0 NormalX=0 NormalY=0 NormalZ=1 AngleXU=0 Radius=0.254
    g82: Circle CenterX=30.48 CenterY=43.18 CenterZ=0 NormalX=0 NormalY=0 NormalZ=1 AngleXU=0 Radius=0.254
    g83: Circle CenterX=24.8708 CenterY=39.4123 CenterZ=0 NormalX=0 NormalY=0 NormalZ=1 AngleXU=0 Radius=0.254
    g84: Circle CenterX=34.925 CenterY=68.7917 CenterZ=0 NormalX=0 NormalY=0 NormalZ=1 AngleXU=0 Radius=0.254
    g85: Circle CenterX=45.72 CenterY=99.06 CenterZ=0 NormalX=0 NormalY=0 NormalZ=1 AngleXU=0 Radius=0.4445
    g86: Circle CenterX=33.02 CenterY=60.325 CenterZ=0 NormalX=0 NormalY=0 NormalZ=1 AngleXU=0 Radius=0.254
    g87: Circle CenterX=38.735 CenterY=1.905 CenterZ=0 NormalX=0 NormalY=0 NormalZ=1 AngleXU=0 Radius=0.508
    g88: Circle CenterX=29.6968 CenterY=63.0555 CenterZ=0 NormalX=0 NormalY=0 NormalZ=1 AngleXU=0 Radius=0.508
    g89: Circle CenterX=27.1568 CenterY=63.0555 CenterZ=0 NormalX=0 NormalY=0 NormalZ=1 AngleXU=0 Radius=0.508
    g90: Circle CenterX=17.78 CenterY=69.85 CenterZ=0 NormalX=0 NormalY=0 NormalZ=1 AngleXU=0 Radius=0.3175
    g91: Circle CenterX=29.9508 CenterY=67.3312 CenterZ=0 NormalX=0 NormalY=0 NormalZ=1 AngleXU=0 Radius=0.254
    g92: Circle CenterX=23.9183 CenterY=66.8232 CenterZ=0 NormalX=0 NormalY=0 NormalZ=1 AngleXU=0 Radius=0.254
    g93: Circle CenterX=4.99533 CenterY=66.04 CenterZ=0 NormalX=0 NormalY=0 NormalZ=1 AngleXU=0 Radius=1.5875
    g94: Circle CenterX=11.0067 CenterY=66.04 CenterZ=0 NormalX=0 NormalY=0 NormalZ=1 AngleXU=0 Radius=1.905
    g95: Circle CenterX=8.001 CenterY=61.341 CenterZ=0 NormalX=0 NormalY=0 NormalZ=1 AngleXU=0 Radius=1.5875
    g96: Circle CenterX=11.5358 CenterY=87.9687 CenterZ=0 NormalX=0 NormalY=0 NormalZ=1 AngleXU=0 Radius=0.656167
    g97: Circle CenterX=10.2764 CenterY=95.9697 CenterZ=0 NormalX=0 NormalY=0 NormalZ=1 AngleXU=0 Radius=0.661458
    g98: Circle CenterX=7.02733 CenterY=91.9692 CenterZ=0 NormalX=0 NormalY=0 NormalZ=1 AngleXU=0 Radius=0.656167
    g99: Circle CenterX=7.53533 CenterY=84.7302 CenterZ=0 NormalX=0 NormalY=0 NormalZ=1 AngleXU=0 Radius=1.5875
    g100: Circle CenterX=7.53533 CenterY=99.2293 CenterZ=0 NormalX=0 NormalY=0 NormalZ=1 AngleXU=0 Radius=1.5875
    g101: Circle CenterX=13.335 CenterY=84.0528 CenterZ=0 NormalX=0 NormalY=0 NormalZ=1 AngleXU=0 Radius=0.254
    g102: Circle CenterX=33.02 CenterY=64.135 CenterZ=0 NormalX=0 NormalY=0 NormalZ=1 AngleXU=0 Radius=0.254
    g103: Circle CenterX=17.145 CenterY=34.29 CenterZ=0 NormalX=0 NormalY=0 NormalZ=1 AngleXU=0 Radius=0.254
    g104: Circle CenterX=38.1 CenterY=21.59 CenterZ=0 NormalX=0 NormalY=0 NormalZ=1 AngleXU=0 Radius=0.254
    g105: Circle CenterX=35.56 CenterY=27.0722 CenterZ=0 NormalX=0 NormalY=0 NormalZ=1 AngleXU=0 Radius=0.254
    g106: Circle CenterX=38.1 CenterY=24.765 CenterZ=0 NormalX=0 NormalY=0 NormalZ=1 AngleXU=0 Radius=0.254
    g107: Circle CenterX=38.1 CenterY=28.575 CenterZ=0 NormalX=0 NormalY=0 NormalZ=1 AngleXU=0 Radius=0.254
    g108: Circle CenterX=20.955 CenterY=33.655 CenterZ=0 NormalX=0 NormalY=0 NormalZ=1 AngleXU=0 Radius=0.254
    g109: Circle CenterX=43.815 CenterY=31.115 CenterZ=0 NormalX=0 NormalY=0 NormalZ=1 AngleXU=0 Radius=0.254
    g110: Circle CenterX=45.085 CenterY=9.525 CenterZ=0 NormalX=0 NormalY=0 NormalZ=1 AngleXU=0 Radius=1.5875
    g111: Circle CenterX=45.085 CenterY=92.075 CenterZ=0 NormalX=0 NormalY=0 NormalZ=1 AngleXU=0 Radius=1.5875
    g112: Circle CenterX=35.814 CenterY=70.0617 CenterZ=0 NormalX=0 NormalY=0 NormalZ=1 AngleXU=0 Radius=0.254
    g113: Circle CenterX=3.81 CenterY=95.25 CenterZ=0 NormalX=0 NormalY=0 NormalZ=1 AngleXU=0 Radius=1.5875
    g114: Circle CenterX=37.465 CenterY=37.465 CenterZ=0 NormalX=0 NormalY=0 NormalZ=1 AngleXU=0 Radius=0.254
    g115: Circle CenterX=21.59 CenterY=99.06 CenterZ=0 NormalX=0 NormalY=0 NormalZ=1 AngleXU=0 Radius=0.4445
    g116: Circle CenterX=35.814 CenterY=13.335 CenterZ=0 NormalX=0 NormalY=0 NormalZ=1 AngleXU=0 Radius=0.254
    g117: Circle CenterX=28.829 CenterY=21.59 CenterZ=0 NormalX=0 NormalY=0 NormalZ=1 AngleXU=0 Radius=0.254
    g118: Circle CenterX=33.401 CenterY=21.59 CenterZ=0 NormalX=0 NormalY=0 NormalZ=1 AngleXU=0 Radius=0.254
    g119: Circle CenterX=35.941 CenterY=22.86 CenterZ=0 NormalX=0 NormalY=0 NormalZ=1 AngleXU=0 Radius=0.254
    g120: Circle CenterX=32.131 CenterY=22.86 CenterZ=0 NormalX=0 NormalY=0 NormalZ=1 AngleXU=0 Radius=0.254
    g121: Circle CenterX=18.796 CenterY=17.7377 CenterZ=0 NormalX=0 NormalY=0 NormalZ=1 AngleXU=0 Radius=0.254
    g122: Circle CenterX=28.2575 CenterY=12.5942 CenterZ=0 NormalX=0 NormalY=0 NormalZ=1 AngleXU=0 Radius=0.254
    g123: Circle CenterX=20.955 CenterY=19.685 CenterZ=0 NormalX=0 NormalY=0 NormalZ=1 AngleXU=0 Radius=0.254
    g124: Circle CenterX=24.765 CenterY=10.16 CenterZ=0 NormalX=0 NormalY=0 NormalZ=1 AngleXU=0 Radius=0.254
    g125: Circle CenterX=16.5523 CenterY=12.065 CenterZ=0 NormalX=0 NormalY=0 NormalZ=1 AngleXU=0 Radius=0.254
    g126: Circle CenterX=16.4888 CenterY=16.51 CenterZ=0 NormalX=0 NormalY=0 NormalZ=1 AngleXU=0 Radius=0.254
    g127: Circle CenterX=19.685 CenterY=10.16 CenterZ=0 NormalX=0 NormalY=0 NormalZ=1 AngleXU=0 Radius=0.254
    g128: Circle CenterX=39.37 CenterY=11.43 CenterZ=0 NormalX=0 NormalY=0 NormalZ=1 AngleXU=0 Radius=0.254
    g129: Circle CenterX=33.655 CenterY=99.06 CenterZ=0 NormalX=0 NormalY=0 NormalZ=1 AngleXU=0 Radius=0.508
    g130: Circle CenterX=3.81 CenterY=19.05 CenterZ=0 NormalX=0 NormalY=0 NormalZ=1 AngleXU=0 Radius=1.5875
    g131: Circle CenterX=15.24 CenterY=40.6188 CenterZ=0 NormalX=0 NormalY=0 NormalZ=1 AngleXU=0 Radius=1.5875
    g132: Circle CenterX=42.3122 CenterY=84.455 CenterZ=0 NormalX=0 NormalY=0 NormalZ=1 AngleXU=0 Radius=0.254
    g133: Circle CenterX=40.8517 CenterY=80.01 CenterZ=0 NormalX=0 NormalY=0 NormalZ=1 AngleXU=0 Radius=0.254
    g134: Circle CenterX=40.8517 CenterY=83.3332 CenterZ=0 NormalX=0 NormalY=0 NormalZ=1 AngleXU=0 Radius=0.254
    g135: Circle CenterX=37.6767 CenterY=82.4865 CenterZ=0 NormalX=0 NormalY=0 NormalZ=1 AngleXU=0 Radius=0.254
    g136: Circle CenterX=30.6917 CenterY=81.915 CenterZ=0 NormalX=0 NormalY=0 NormalZ=1 AngleXU=0 Radius=0.254
    g137: Circle CenterX=31.5807 CenterY=83.185 CenterZ=0 NormalX=0 NormalY=0 NormalZ=1 AngleXU=0 Radius=0.254
    g138: Circle CenterX=38.735 CenterY=92.075 CenterZ=0 NormalX=0 NormalY=0 NormalZ=1 AngleXU=0 Radius=0.254
    g139: Circle CenterX=3.048 CenterY=3.048 CenterZ=0 NormalX=0 NormalY=0 NormalZ=1 AngleXU=0 Radius=2.43417
    g140: Circle CenterX=2.54 CenterY=77.47 CenterZ=0 NormalX=0 NormalY=0 NormalZ=1 AngleXU=0 Radius=0.254
    g141: Circle CenterX=26.0244 CenterY=85.7673 CenterZ=0 NormalX=0 NormalY=0 NormalZ=1 AngleXU=0 Radius=0.365125
    g142: Circle CenterX=23.4844 CenterY=85.7673 CenterZ=0 NormalX=0 NormalY=0 NormalZ=1 AngleXU=0 Radius=0.365125
    g143: Circle CenterX=24.765 CenterY=84.0317 CenterZ=0 NormalX=0 NormalY=0 NormalZ=1 AngleXU=0 Radius=0.254
    g144: Circle CenterX=18.415 CenterY=79.375 CenterZ=0 NormalX=0 NormalY=0 NormalZ=1 AngleXU=0 Radius=0.254
    g145: Circle CenterX=23.495 CenterY=81.1318 CenterZ=0 NormalX=0 NormalY=0 NormalZ=1 AngleXU=0 Radius=0.254
    g146: Circle CenterX=2.56117 CenterY=51.8372 CenterZ=0 NormalX=0 NormalY=0 NormalZ=1 AngleXU=0 Radius=0.4445
    g147: Circle CenterX=2.56117 CenterY=47.8367 CenterZ=0 NormalX=0 NormalY=0 NormalZ=1 AngleXU=0 Radius=0.4445
    g148: Circle CenterX=2.55058 CenterY=45.7306 CenterZ=0 NormalX=0 NormalY=0 NormalZ=1 AngleXU=0 Radius=0.772583
    g149: Circle CenterX=2.55058 CenterY=53.9221 CenterZ=0 NormalX=0 NormalY=0 NormalZ=1 AngleXU=0 Radius=0.772583
    g150: Circle CenterX=2.56117 CenterY=49.8263 CenterZ=0 NormalX=0 NormalY=0 NormalZ=1 AngleXU=0 Radius=0.4445
    g151: Circle CenterX=2.56117 CenterY=39.1372 CenterZ=0 NormalX=0 NormalY=0 NormalZ=1 AngleXU=0 Radius=0.4445
    g152: Circle CenterX=2.56117 CenterY=35.1367 CenterZ=0 NormalX=0 NormalY=0 NormalZ=1 AngleXU=0 Radius=0.4445
    g153: Circle CenterX=2.55058 CenterY=33.0306 CenterZ=0 NormalX=0 NormalY=0 NormalZ=1 AngleXU=0 Radius=0.772583
    g154: Circle CenterX=2.55058 CenterY=41.2327 CenterZ=0 NormalX=0 NormalY=0 NormalZ=1 AngleXU=0 Radius=0.777875
    g155: Circle CenterX=2.56117 CenterY=37.1263 CenterZ=0 NormalX=0 NormalY=0 NormalZ=1 AngleXU=0 Radius=0.4445
    g156: Circle CenterX=22.86 CenterY=88.265 CenterZ=0 NormalX=0 NormalY=0 NormalZ=1 AngleXU=0 Radius=0.254
    g157: Circle CenterX=6.35 CenterY=39.9203 CenterZ=0 NormalX=0 NormalY=0 NormalZ=1 AngleXU=0 Radius=0.254
    g158: Circle CenterX=31.115 CenterY=10.795 CenterZ=0 NormalX=0 NormalY=0 NormalZ=1 AngleXU=0 Radius=0.254
    g159: Circle CenterX=20.0025 CenterY=58.0496 CenterZ=0 NormalX=0 NormalY=0 NormalZ=1 AngleXU=0 Radius=0.365125
    g160: Circle CenterX=4.445 CenterY=57.785 CenterZ=0 NormalX=0 NormalY=0 NormalZ=1 AngleXU=0 Radius=0.254
    g161: Circle CenterX=6.35 CenterY=46.99 CenterZ=0 NormalX=0 NormalY=0 NormalZ=1 AngleXU=0 Radius=0.254
    g162: Circle CenterX=8.509 CenterY=57.8062 CenterZ=0 NormalX=0 NormalY=0 NormalZ=1 AngleXU=0 Radius=0.254
    g163: Circle CenterX=14.605 CenterY=57.15 CenterZ=0 NormalX=0 NormalY=0 NormalZ=1 AngleXU=0 Radius=0.254
    g164: Circle CenterX=24.13 CenterY=72.5593 CenterZ=0 NormalX=0 NormalY=0 NormalZ=1 AngleXU=0 Radius=0.254
    g165: Circle CenterX=13.335 CenterY=74.295 CenterZ=0 NormalX=0 NormalY=0 NormalZ=1 AngleXU=0 Radius=0.254
    g166: Circle CenterX=20.9444 CenterY=64.1244 CenterZ=0 NormalX=0 NormalY=0 NormalZ=1 AngleXU=0 Radius=0.370417
    g167: Circle CenterX=9.525 CenterY=69.85 CenterZ=0 NormalX=0 NormalY=0 NormalZ=1 AngleXU=0 Radius=0.508
    g168: Circle CenterX=1.905 CenterY=69.85 CenterZ=0 NormalX=0 NormalY=0 NormalZ=1 AngleXU=0 Radius=0.508
    g169: Circle CenterX=49.53 CenterY=100.33 CenterZ=0 NormalX=0 NormalY=0 NormalZ=1 AngleXU=0 Radius=0.4445
    g170: Circle CenterX=47.9213 CenterY=99.06 CenterZ=0 NormalX=0 NormalY=0 NormalZ=1 AngleXU=0 Radius=0.4445
    g171: Circle CenterX=49.53 CenterY=97.79 CenterZ=0 NormalX=0 NormalY=0 NormalZ=1 AngleXU=0 Radius=0.4445
    g172: Circle CenterX=47.9213 CenterY=96.52 CenterZ=0 NormalX=0 NormalY=0 NormalZ=1 AngleXU=0 Radius=0.4445
    g173: Circle CenterX=49.53 CenterY=86.995 CenterZ=0 NormalX=0 NormalY=0 NormalZ=1 AngleXU=0 Radius=0.4445
    g174: Circle CenterX=47.9213 CenterY=85.725 CenterZ=0 NormalX=0 NormalY=0 NormalZ=1 AngleXU=0 Radius=0.4445
    g175: Circle CenterX=49.53 CenterY=84.455 CenterZ=0 NormalX=0 NormalY=0 NormalZ=1 AngleXU=0 Radius=0.4445
    g176: Circle CenterX=47.9213 CenterY=83.185 CenterZ=0 NormalX=0 NormalY=0 NormalZ=1 AngleXU=0 Radius=0.4445
    g177: Circle CenterX=49.53 CenterY=65.405 CenterZ=0 NormalX=0 NormalY=0 NormalZ=1 AngleXU=0 Radius=0.4445
    g178: Circle CenterX=47.9213 CenterY=64.135 CenterZ=0 NormalX=0 NormalY=0 NormalZ=1 AngleXU=0 Radius=0.4445
    g179: Circle CenterX=49.53 CenterY=62.865 CenterZ=0 NormalX=0 NormalY=0 NormalZ=1 AngleXU=0 Radius=0.4445
    g180: Circle CenterX=47.9213 CenterY=61.595 CenterZ=0 NormalX=0 NormalY=0 NormalZ=1 AngleXU=0 Radius=0.4445
    g181: Circle CenterX=49.53 CenterY=52.07 CenterZ=0 NormalX=0 NormalY=0 NormalZ=1 AngleXU=0 Radius=0.4445
    g182: Circle CenterX=47.9213 CenterY=50.8 CenterZ=0 NormalX=0 NormalY=0 NormalZ=1 AngleXU=0 Radius=0.4445
    g183: Circle CenterX=49.53 CenterY=49.53 CenterZ=0 NormalX=0 NormalY=0 NormalZ=1 AngleXU=0 Radius=0.4445
    g184: Circle CenterX=47.9213 CenterY=48.26 CenterZ=0 NormalX=0 NormalY=0 NormalZ=1 AngleXU=0 Radius=0.4445
    g185: Circle CenterX=49.53 CenterY=30.48 CenterZ=0 NormalX=0 NormalY=0 NormalZ=1 AngleXU=0 Radius=0.4445
    g186: Circle CenterX=47.9213 CenterY=29.21 CenterZ=0 NormalX=0 NormalY=0 NormalZ=1 AngleXU=0 Radius=0.4445
    g187: Circle CenterX=49.53 CenterY=27.94 CenterZ=0 NormalX=0 NormalY=0 NormalZ=1 AngleXU=0 Radius=0.4445
    g188: Circle CenterX=47.9213 CenterY=26.67 CenterZ=0 NormalX=0 NormalY=0 NormalZ=1 AngleXU=0 Radius=0.4445
    g189: Circle CenterX=49.53 CenterY=17.145 CenterZ=0 NormalX=0 NormalY=0 NormalZ=1 AngleXU=0 Radius=0.4445
    g190: Circle CenterX=47.9213 CenterY=15.875 CenterZ=0 NormalX=0 NormalY=0 NormalZ=1 AngleXU=0 Radius=0.4445
    g191: Circle CenterX=49.53 CenterY=14.605 CenterZ=0 NormalX=0 NormalY=0 NormalZ=1 AngleXU=0 Radius=0.4445
    g192: Circle CenterX=47.9213 CenterY=13.335 CenterZ=0 NormalX=0 NormalY=0 NormalZ=1 AngleXU=0 Radius=0.4445
    g193: Circle CenterX=45.085 CenterY=74.93 CenterZ=0 NormalX=0 NormalY=0 NormalZ=1 AngleXU=0 Radius=0.254
    g194: Circle CenterX=46.99 CenterY=56.515 CenterZ=0 NormalX=0 NormalY=0 NormalZ=1 AngleXU=0 Radius=0.254
    g195: Circle CenterX=44.45 CenterY=55.88 CenterZ=0 NormalX=0 NormalY=0 NormalZ=1 AngleXU=0 Radius=0.254
    g196: Circle CenterX=41.9206 CenterY=52.07 CenterZ=0 NormalX=0 NormalY=0 NormalZ=1 AngleXU=0 Radius=0.174625
FEATURE [PartDesign::Pocket] Holes
  BaseFeature = -> Main
  Direction = (0,0,-1)
  Length = 3.556
  Length2 = 5
  Profile = -> HoleSketch
  Refine = true
  Reversed = true
  Suppressed = false
  Type = 0
FEATURE [PartDesign::Body] Body  label="pcb imported"
  AllowCompound = false
  Group = -> [MainSketch,Main,HoleSketch,Holes]
  Origin = -> Origin
  Tip = -> Holes
FEATURE [App::Link] pcb_imported  label="pcb imported001"
  LinkedObject = -> Body
FEATURE [App::FeaturePython] GroundedJoint  # Assembly grounded joint (typed FeaturePython)
  ObjectToGround = -> pcb_imported
FEATURE [Part::Feature] Part__Feature  label="WP154A4SUREQBFZGC"
  shape: bbox 5.9 x 5.487 x 33.1 mm, 95 faces (baked)
FEATURE [App::Link] WP154A4SUREQBFZGC  label="WP154A4SUREQBFZGC001"
  LinkPlacement = pos=(54.356,15.113,4.572) rot=(0,1,0;1.5708rad)
  LinkedObject = -> Part__Feature
  Placement = pos=(54.356,15.113,4.572) rot=(0,1,0;1.5708rad)
FEATURE [App::FeaturePython] Joint  label="Fixed"  # Assembly joint (typed FeaturePython)
  Activated = true
  AngleMax = 0
  AngleMin = 0
  Detach1 = false
  Detach2 = false
  Distance = 0
  Distance2 = 0
  EnableAngleMax = false
  EnableAngleMin = false
  EnableLengthMax = false
  EnableLengthMin = false
  JointType = 0 (Fixed)
  LengthMax = 0
  LengthMin = 0
  Offset1 = pos=(4.572,-15.113,-54.356) rot=(0.707107,0,0.707107;3.14159rad)
  Placement1 = pos=(4.572,-15.113,-54.356) rot=(0.707107,0,0.707107;3.14159rad)
  Reference1 = -> Assembly [WP154A4SUREQBFZGC.,WP154A4SUREQBFZGC.]
  Reference2 = -> Assembly [pcb_imported.,pcb_imported.]
FEATURE [App::Link] WP154A4SUREQBFZGC001  label="WP154A4SUREQBFZGC002"
  LinkPlacement = pos=(54.356,28.448,4.572) rot=(0,1,0;1.5708rad)
  LinkedObject = -> Part__Feature
  Placement = pos=(54.356,28.448,4.572) rot=(0,1,0;1.5708rad)
FEATURE [App::FeaturePython] Joint001  label="Fixed001"  # Assembly joint (typed FeaturePython)
  Activated = true
  AngleMax = 0
  AngleMin = 0
  Detach1 = false
  Detach2 = false
  Distance = 0
  Distance2 = 0
  EnableAngleMax = false
  EnableAngleMin = false
  EnableLengthMax = false
  EnableLengthMin = false
  JointType = 0 (Fixed)
  LengthMax = 0
  LengthMin = 0
  Offset1 = pos=(0,-13.335,0) rot=(1,0,0;3.14159rad)
  Placement1 = pos=(0,-13.335,0) rot=(1,0,0;3.14159rad)
  Reference1 = -> Assembly [WP154A4SUREQBFZGC001.,WP154A4SUREQBFZGC001.]
  Reference2 = -> Assembly [WP154A4SUREQBFZGC.,WP154A4SUREQBFZGC.]
FEATURE [App::Link] WP154A4SUREQBFZGC002  label="WP154A4SUREQBFZGC003"
  LinkPlacement = pos=(54.356,50.038,4.572) rot=(0,1,0;1.5708rad)
  LinkedObject = -> Part__Feature
  Placement = pos=(54.356,50.038,4.572) rot=(0,1,0;1.5708rad)
FEATURE [App::FeaturePython] Joint002  label="Fixed002"  # Assembly joint (typed FeaturePython)
  Activated = true
  AngleMax = 0
  AngleMin = 0
  Detach1 = false
  Detach2 = false
  Distance = 0
  Distance2 = 0
  EnableAngleMax = false
  EnableAngleMin = false
  EnableLengthMax = false
  EnableLengthMin = false
  JointType = 0 (Fixed)
  LengthMax = 0
  LengthMin = 0
  Offset1 = pos=(0,-34.925,0) rot=(0,0,1;0rad)
  Placement1 = pos=(0,-34.925,0) rot=(0,0,1;0rad)
  Reference1 = -> Assembly [WP154A4SUREQBFZGC002.,WP154A4SUREQBFZGC002.]
  Reference2 = -> Assembly [WP154A4SUREQBFZGC.,WP154A4SUREQBFZGC.]
FEATURE [App::Link] WP154A4SUREQBFZGC003  label="WP154A4SUREQBFZGC004"
  LinkPlacement = pos=(54.356,63.373,4.572) rot=(0,1,0;1.5708rad)
  LinkedObject = -> Part__Feature
  Placement = pos=(54.356,63.373,4.572) rot=(0,1,0;1.5708rad)
FEATURE [App::FeaturePython] Joint003  label="Fixed003"  # Assembly joint (typed FeaturePython)
  Activated = true
  AngleMax = 0
  AngleMin = 0
  Detach1 = false
  Detach2 = false
  Distance = 0
  Distance2 = 0
  EnableAngleMax = false
  EnableAngleMin = false
  EnableLengthMax = false
  EnableLengthMin = false
  JointType = 0 (Fixed)
  LengthMax = 0
  LengthMin = 0
  Offset1 = pos=(0,-13.335,0) rot=(0,0,1;0rad)
  Placement1 = pos=(0,-13.335,0) rot=(0,0,1;0rad)
  Reference1 = -> Assembly [WP154A4SUREQBFZGC003.,WP154A4SUREQBFZGC003.]
  Reference2 = -> Assembly [WP154A4SUREQBFZGC002.,WP154A4SUREQBFZGC002.]
FEATURE [App::Link] WP154A4SUREQBFZGC004  label="WP154A4SUREQBFZGC005"
  LinkPlacement = pos=(54.356,84.963,4.572) rot=(0,1,0;1.5708rad)
  LinkedObject = -> Part__Feature
  Placement = pos=(54.356,84.963,4.572) rot=(0,1,0;1.5708rad)
FEATURE [App::FeaturePython] Joint004  label="Fixed004"  # Assembly joint (typed FeaturePython)
  Activated = true
  AngleMax = 0
  AngleMin = 0
  Detach1 = false
  Detach2 = false
  Distance = 0
  Distance2 = 0
  EnableAngleMax = false
  EnableAngleMin = false
  EnableLengthMax = false
  EnableLengthMin = false
  JointType = 0 (Fixed)
  LengthMax = 0
  LengthMin = 0
  Offset1 = pos=(0,34.925,0) rot=(0,0,1;0rad)
  Placement1 = pos=(0,34.925,0) rot=(0,0,1;0rad)
  Reference1 = -> Assembly [WP154A4SUREQBFZGC002.,WP154A4SUREQBFZGC002.]
  Reference2 = -> Assembly [WP154A4SUREQBFZGC004.,WP154A4SUREQBFZGC004.]
FEATURE [App::Link] WP154A4SUREQBFZGC005  label="WP154A4SUREQBFZGC006"
  LinkPlacement = pos=(54.356,98.298,4.572) rot=(0,1,0;1.5708rad)
  LinkedObject = -> Part__Feature
  Placement = pos=(54.356,98.298,4.572) rot=(0,1,0;1.5708rad)
FEATURE [App::FeaturePython] Joint005  label="Fixed005"  # Assembly joint (typed FeaturePython)
  Activated = true
  AngleMax = 0
  AngleMin = 0
  Detach1 = false
  Detach2 = false
  Distance = 0
  Distance2 = 0
  EnableAngleMax = false
  EnableAngleMin = false
  EnableLengthMax = false
  EnableLengthMin = false
  JointType = 0 (Fixed)
  LengthMax = 0
  LengthMin = 0
  Offset1 = pos=(0,-13.335,0) rot=(0,0,1;0rad)
  Placement1 = pos=(0,-13.335,0) rot=(0,0,1;0rad)
  Reference1 = -> Assembly [WP154A4SUREQBFZGC005.,WP154A4SUREQBFZGC005.]
  Reference2 = -> Assembly [WP154A4SUREQBFZGC004.,WP154A4SUREQBFZGC004.]
FEATURE [Part::Feature] Part__Feature003  label="Dual RCA"
  shape: bbox 20.7 x 22.3 x 31.6 mm, 33 faces (baked)
FEATURE [App::Link] Dual_RCA  label="Dual RCA001"
  LinkPlacement = pos=(0.032625,91.9586,15.028) rot=(0,0,-1;1.5708rad)
  LinkedObject = -> Part__Feature003
  Placement = pos=(0.032625,91.9586,15.028) rot=(0,0,-1;1.5708rad)
FEATURE [App::FeaturePython] Joint008  label="Fixed008"  # Assembly joint (typed FeaturePython)
  Activated = true
  AngleMax = 0
  AngleMin = 0
  Detach1 = false
  Detach2 = false
  Distance = 0
  Distance2 = 0
  EnableAngleMax = false
  EnableAngleMin = false
  EnableLengthMax = false
  EnableLengthMin = false
  JointType = 0 (Fixed)
  LengthMax = 0
  LengthMin = 0
  Offset1 = pos=(-13.335,33.909,0) rot=(0,0,1;1.5708rad)
  Placement1 = pos=(7.03262,91.9586,1.778) rot=(0,0,1;1.5708rad)
  Placement2 = pos=(-1.42e-14,7,-13.25) rot=(0,1,0;3.14159rad)
  Reference1 = -> Assembly [pcb_imported.Face5,pcb_imported.Vertex332]
  Reference2 = -> Assembly [Dual_RCA.Face1,Dual_RCA.Edge1]
FEATURE [Part::Feature] Part__Feature004  label="Pro Mini"
  shape: bbox 17.78 x 33.02 x 1.588 mm, 16 faces (baked)
FEATURE [App::Link] Pro_Mini  label="Pro Mini001"
  LinkPlacement = pos=(28.575,39.37,11.938) rot=(0,0,1;4.71239rad)
  LinkedObject = -> Part__Feature004
  Placement = pos=(28.575,39.37,11.938) rot=(0,0,1;4.71239rad)
FEATURE [App::FeaturePython] Joint009  label="Fixed009"  # Assembly joint (typed FeaturePython)
  Activated = true
  AngleMax = 0
  AngleMin = 0
  Detach1 = false
  Detach2 = false
  Distance = 0
  Distance2 = 0
  EnableAngleMax = false
  EnableAngleMin = false
  EnableLengthMax = false
  EnableLengthMin = false
  JointType = 0 (Fixed)
  LengthMax = 0
  LengthMin = 0
  Offset1 = pos=(39.37,-28.575,-11.938) rot=(0,0,1;1.5708rad)
  Placement1 = pos=(39.37,-28.575,-11.938) rot=(0,0,1;1.5708rad)
  Reference1 = -> Assembly [Pro_Mini.,Pro_Mini.]
  Reference2 = -> Assembly [pcb_imported.,pcb_imported.]
FEATURE [Part::Feature] Part__Feature005  label="Body1"
  shape: bbox 8.13 x 5.08 x 8.03 mm, 51 faces (baked)
FEATURE [Part::Feature] Part__Feature006  label="Body2"
  shape: bbox 8.13 x 5.08 x 6.63 mm, 28 faces (baked)
FEATURE [Part::Feature] Part__Feature007  label="Body3"
  shape: bbox 8.13 x 8.61 x 1.39 mm, 44 faces (baked)
FEATURE [Part::Feature] Part__Feature008  label="Body4"
  shape: bbox 6.101 x 6.101 x 6.101 mm, 9 faces (baked)
FEATURE [Part::Feature] Part__Feature009  label="Body5"
  shape: bbox 8 x 11.33 x 3.705 mm, 42 faces (baked)
FEATURE [Part::Feature] Part__Feature010  label="Body6"
  shape: bbox 2.54 x 2.54 x 6 mm, 3 faces (baked)
FEATURE [App::Part] _00SP9B6M6RE__3DModel_STEP_520916  label="800SP9B6M6RE--3DModel-STEP-520916"
  Group = -> [Part__Feature005,Part__Feature006,Part__Feature007,Part__Feature008,Part__Feature009,Part__Feature010]
  Origin = -> Origin002
  Placement = pos=(0,3.05,-1.7005) rot=(0,0,1;0rad)
FEATURE [App::Part] SPST_momentary  label="SPST-momentary"
  Group = -> [_00SP9B6M6RE__3DModel_STEP_520916]
  Origin = -> Origin003
FEATURE [App::Link] SPST_momentary001  label="SPST-momentary001"
  LinkPlacement = pos=(9.02102,11.6417,1.678) rot=(-0.57735,0.57735,0.57735;4.18879rad)
  LinkedObject = -> SPST_momentary
  Placement = pos=(9.02102,11.6417,1.678) rot=(-0.57735,0.57735,0.57735;4.18879rad)
FEATURE [App::FeaturePython] Joint010  label="Fixed010"  # Assembly joint (typed FeaturePython)
  Activated = true
  AngleMax = 0
  AngleMin = 0
  Detach1 = false
  Detach2 = false
  Distance = 0
  Distance2 = 0
  EnableAngleMax = false
  EnableAngleMin = false
  EnableLengthMax = false
  EnableLengthMin = false
  JointType = 0 (Fixed)
  LengthMax = 0
  LengthMin = 0
  Offset1 = pos=(-14.224,-6.096,0) rot=(0,0,1;3.14159rad)
  Placement1 = pos=(4.826,11.6417,1.778) rot=(0,0,1;3.14159rad)
  Placement2 = pos=(2e-16,-2.95,5.89552) rot=(0.57735,0.57735,0.57735;4.18879rad)
  Reference1 = -> Assembly [pcb_imported.Face5,pcb_imported.Vertex223]
  Reference2 = -> Assembly [SPST_momentary001._00SP9B6M6RE__3DModel_STEP_520916.Part__Feature009.Face24,SPST_momentary001._00SP9B6M6RE__3DModel_STEP_520916.Part__Feature009.Face24]
FEATURE [Part::Feature] Part__Feature011  label="3pinconnector-640441-3"
  shape: bbox 7.62 x 7.087 x 13.21 mm, 307 faces (baked)
FEATURE [App::Link] _pinconnector_640441_3  label="3pinconnector-640441-004"
  LinkPlacement = pos=(45.7412,2.54,1.778) rot=(0,1,0;3.14159rad)
  LinkedObject = -> Part__Feature011
  Placement = pos=(45.7412,2.54,1.778) rot=(0,1,0;3.14159rad)
FEATURE [App::FeaturePython] Joint011  label="Fixed011"  # Assembly joint (typed FeaturePython)
  Activated = true
  AngleMax = 0
  AngleMin = 0
  Detach1 = false
  Detach2 = false
  Distance = 0
  Distance2 = 0
  EnableAngleMax = false
  EnableAngleMin = false
  EnableLengthMax = false
  EnableLengthMin = false
  JointType = 0 (Fixed)
  LengthMax = 0
  LengthMin = 0
  Offset1 = pos=(41.148,1.27,0) rot=(0,0,1;3.14159rad)
  Placement1 = pos=(40.259,0.508,2e-16) rot=(0,0,1;3.14159rad)
  Placement2 = pos=(5.48217,3.048,1.778) rot=(0,0,1;0rad)
  Reference1 = -> Assembly [_pinconnector_640441_3.Face186,_pinconnector_640441_3.Vertex340]
  Reference2 = -> Assembly [pcb_imported.Face5,pcb_imported.Vertex206]
FEATURE [App::Link] _pinconnector_640441_004  label="3pinconnector-640441-005"
  LinkPlacement = pos=(4.445,29.845,1.778) rot=(0,1,0;3.14159rad)
  LinkedObject = -> Part__Feature011
  Placement = pos=(4.445,29.845,1.778) rot=(0,1,0;3.14159rad)
FEATURE [App::FeaturePython] Joint012  label="Fixed012"  # Assembly joint (typed FeaturePython)
  Activated = true
  AngleMax = 0
  AngleMin = 0
  Detach1 = false
  Detach2 = false
  Distance = 0
  Distance2 = 0
  EnableAngleMax = false
  EnableAngleMin = false
  EnableLengthMax = false
  EnableLengthMin = false
  JointType = 0 (Fixed)
  LengthMax = 0
  LengthMin = 0
  Offset1 = pos=(-23.749,-2.794,0) rot=(0,0,1;3.14159rad)
  Placement1 = pos=(2.794,29.083,1.778) rot=(0,0,1;3.14159rad)
  Placement2 = pos=(1.651,-0.762,2e-16) rot=(0,0,1;0rad)
  Reference1 = -> Assembly [pcb_imported.Face5,pcb_imported.Vertex284]
  Reference2 = -> Assembly [_pinconnector_640441_004.Face186,_pinconnector_640441_004.Vertex328]
FEATURE [App::Link] _pinconnector_640441_005  label="3pinconnector-640441-006"
  LinkPlacement = pos=(33.0962,92.7862,1.778) rot=(0,1,0;3.14159rad)
  LinkedObject = -> Part__Feature011
  Placement = pos=(33.0962,92.7862,1.778) rot=(0,1,0;3.14159rad)
FEATURE [App::FeaturePython] Joint013  label="Fixed013"  # Assembly joint (typed FeaturePython)
  Activated = true
  AngleMax = 0
  AngleMin = 0
  Detach1 = false
  Detach2 = false
  Distance = 0
  Distance2 = 0
  EnableAngleMax = false
  EnableAngleMin = false
  EnableLengthMax = false
  EnableLengthMin = false
  JointType = 0 (Fixed)
  LengthMax = 0
  LengthMin = 0
  Offset1 = pos=(18.8722,44.9072,0) rot=(0,0,1;3.14159rad)
  Placement1 = pos=(32.2072,92.0242,1.778) rot=(0,0,1;3.14159rad)
  Placement2 = pos=(0.889,-0.762,0) rot=(0,0,1;0rad)
  Reference1 = -> Assembly [pcb_imported.Face5,pcb_imported.Edge49]
  Reference2 = -> Assembly [_pinconnector_640441_005.Face186,_pinconnector_640441_005.Vertex338]
FEATURE [Part::Feature] Part__Feature012  label="CUI_PJ-202A"
  shape: bbox 14.41 x 14.87 x 9.41 mm, 65 faces (baked)
FEATURE [App::Link] CUI_PJ_202A  label="CUI_PJ-202A001"
  LinkPlacement = pos=(-2.69501,66.04,8.278) rot=(0,0.707107,0.707107;3.14159rad)
  LinkedObject = -> Part__Feature012
  Placement = pos=(-2.69501,66.04,8.278) rot=(0,0.707107,0.707107;3.14159rad)
FEATURE [App::FeaturePython] Joint014  label="Fixed014"  # Assembly joint (typed FeaturePython)
  Activated = true
  AngleMax = 0
  AngleMin = 0
  Detach1 = false
  Detach2 = false
  Distance = 0
  Distance2 = 0
  EnableAngleMax = false
  EnableAngleMin = false
  EnableLengthMax = false
  EnableLengthMin = false
  JointType = 0 (Fixed)
  LengthMax = 0
  LengthMin = 0
  Offset1 = pos=(-15.24,40.64,0) rot=(0,0,-1;1.5708rad)
  Placement1 = pos=(4.318,66.04,1.778) rot=(0,0,-1;1.5708rad)
  Placement2 = pos=(-7.01301,-6.5,0) rot=(0.57735,0.57735,-0.57735;2.0944rad)
  Reference1 = -> Assembly [pcb_imported.Face5,pcb_imported.Vertex225]
  Reference2 = -> Assembly [CUI_PJ_202A.Face5,CUI_PJ_202A.Face5]
FEATURE [Part::Feature] Part__Feature013  label="SLW-864547-5A-RA-D"
  shape: bbox 8.6 x 9.5 x 7.5 mm, 89 faces (baked)
FEATURE [App::Link] SLW_864547_5A_RA_D  label="SLW-864547-5A-RA-D001"
  LinkPlacement = pos=(2.563,37.056,1.72323) rot=(0,0,1;4.71239rad)
  LinkedObject = -> Part__Feature013
  Placement = pos=(2.563,37.056,1.72323) rot=(0,0,1;4.71239rad)
FEATURE [App::FeaturePython] Joint015  label="Fixed015"  # Assembly joint (typed FeaturePython)
  Activated = true
  AngleMax = 0
  AngleMin = 0
  Detach1 = false
  Detach2 = false
  Distance = 0
  Distance2 = 0
  EnableAngleMax = false
  EnableAngleMin = false
  EnableLengthMax = false
  EnableLengthMin = false
  JointType = 0 (Fixed)
  LengthMax = 0
  LengthMin = 0
  Offset1 = pos=(13.716,26.416,0) rot=(0,0,1;1.5708rad)
  Placement1 = pos=(15.466,26.266,0.0547674) rot=(0,0,-1;4.71239rad)
  Placement2 = pos=(28.829,21.59,1.778) rot=(0,0,1;0rad)
  Reference1 = -> Assembly [SLW_864547_5A_RA_D.Face17,SLW_864547_5A_RA_D.Vertex24]
  Reference2 = -> Assembly [pcb_imported.Face5,pcb_imported.Edge60]
FEATURE [App::Link] SLW_864547_5A_RA_D001  label="SLW-864547-5A-RA-D002"
  LinkPlacement = pos=(2.563,49.756,1.72323) rot=(0,0,1;4.71239rad)
  LinkedObject = -> Part__Feature013
  Placement = pos=(2.563,49.756,1.72323) rot=(0,0,1;4.71239rad)
FEATURE [App::FeaturePython] Joint016  label="Fixed016"  # Assembly joint (typed FeaturePython)
  Activated = true
  AngleMax = 0
  AngleMin = 0
  Detach1 = false
  Detach2 = false
  Distance = 0
  Distance2 = 0
  EnableAngleMax = false
  EnableAngleMin = false
  EnableLengthMax = false
  EnableLengthMin = false
  JointType = 0 (Fixed)
  LengthMax = 0
  LengthMin = 0
  Offset1 = pos=(-12.7,0,0) rot=(0,0,1;0rad)
  Placement1 = pos=(-12.7,0,0) rot=(0,0,1;0rad)
  Reference1 = -> Assembly [SLW_864547_5A_RA_D.,SLW_864547_5A_RA_D.]
  Reference2 = -> Assembly [SLW_864547_5A_RA_D001.,SLW_864547_5A_RA_D001.]
FEATURE [Part::Feature] Part__Feature014  label="quiik"
  Placement = pos=(-3.68878,1.645,-3.606e-13) rot=(0,1,0;1.5708rad)
  shape: bbox 4.95 x 2.96 x 6 mm, 217 faces (baked)
FEATURE [Part::Feature] Part__Feature015  label="USB-C"
  Placement = pos=(-33.8738,-1.46186,-5.52737) rot=(0,-1,0;1.5708rad)
  shape: bbox 7.904 x 3.166 x 11.6 mm, 550 faces (baked)
FEATURE [Part::Feature] Part__Feature016  label="pcb-ft232"
  Placement = pos=(0.206219,-1.323e-13,11.43) rot=(0,0,1;0rad)
  shape: bbox 38.1 x 2 x 22.86 mm, 6 faces (baked)
FEATURE [App::Link] Ft232H_2_assembly001  label="Ft232H-2-assembly001"
  LinkPlacement = pos=(37.8726,15.185,11.684) rot=(1,0,0;1.5708rad)
  LinkedObject = -> Ft232H_2_assembly
  Placement = pos=(37.8726,15.185,11.684) rot=(1,0,0;1.5708rad)
FEATURE [App::FeaturePython] Joint017  label="Fixed017"  # Assembly joint (typed FeaturePython)
  Activated = true
  AngleMax = 0
  AngleMin = 0
  Detach1 = false
  Detach2 = false
  Distance = 0
  Distance2 = 0
  EnableAngleMax = false
  EnableAngleMin = false
  EnableLengthMax = false
  EnableLengthMin = false
  JointType = 0 (Fixed)
  LengthMax = 0
  LengthMin = 0
  Offset1 = pos=(-52.1462,11.176,-9.906) rot=(0,0,1;1.5708rad)
  Placement1 = pos=(-7.874,-9.906,-63.5762) rot=(1,0,0;4.71239rad)
  Placement2 = pos=(30.2048,67.3312,1.778) rot=(0,0,1;0rad)
  Reference1 = -> Assembly [Ft232H_2_assembly001.Part__Feature016.Face6,Ft232H_2_assembly001.Part__Feature016.Face6]
  Reference2 = -> Assembly [pcb_imported.Face5,pcb_imported.Vertex359]
FEATURE [Assembly::JointGroup] Joints
  Group = -> [GroundedJoint,Joint,Joint001,Joint002,Joint003,Joint004,Joint005,Joint008,Joint009,Joint010,Joint011,Joint012,Joint013,Joint014,Joint015,Joint016,Joint017]
FEATURE [Assembly::AssemblyObject] Assembly  label="PCB Assembly"
  Group = -> [Joints,pcb_imported,GroundedJoint,WP154A4SUREQBFZGC,Joint,WP154A4SUREQBFZGC001,Joint001,WP154A4SUREQBFZGC002,Joint002,WP154A4SUREQBFZGC003,Joint003,WP154A4SUREQBFZGC004,Joint004,WP154A4SUREQBFZGC005,Joint005,Dual_RCA,Joint008,Pro_Mini,Joint009,SPST_momentary001,Joint010,_pinconnector_640441_3,Joint011,_pinconnector_640441_004,Joint012,_pinconnector_640441_005,Joint013,CUI_PJ_202A,Joint014,+6 more]
  Origin = -> Origin001
  Type = Assembly
FEATURE [PartDesign::SubShapeBinder] Binder
  BindCopyOnChange = 0
  BindMode = 0
  ClaimChildren = false
  Context = -> Assembly [Ft232H_2_assembly001.Body001.Binder.]
  Fuse = false
  MakeFace = true
  OffsetFill = false
  OffsetIntersection = false
  OffsetJoinType = 0
  OffsetOpenResult = false
  PartialLoad = false
  Refine = true
  Relative = true
  Support = -> [Part__Feature016]
  _Version = 2
FEATURE [Sketcher::SketchObject] Sketch
  ArcFitTolerance = 1e-06
  AttachmentSupport = -> [Binder]
  ExternalGeometry = -> [Binder]
  FullyConstrained = true
  MakeInternals = false
  MapMode = 5
  Placement = pos=(0,-1.32e-13,0) rot=(1,0,0;1.5708rad)
  sketch-geometry (10):
    g0: LineSegment [constr] StartX=-31.5438 StartY=10.16 StartZ=0 EndX=-31.5438 EndY=-10.16 EndZ=0
    g1: LineSegment [constr] StartX=-31.5438 StartY=-10.16 StartZ=0 EndX=-6.14378 EndY=-10.16 EndZ=0
    g2: LineSegment [constr] StartX=-6.14378 StartY=-10.16 StartZ=0 EndX=-6.14378 EndY=10.16 EndZ=0
    g3: LineSegment [constr] StartX=-6.14378 StartY=10.16 StartZ=0 EndX=-31.5438 EndY=10.16 EndZ=0
    g4: GeomPoint [constr] X=-37.8938 Y=-3.968e-13 Z=0
    g5: GeomPoint [constr] X=-31.5438 Y=-3.968e-13 Z=0
    g6: GeomPoint [constr] X=-18.8438 Y=11.43 Z=0
    g7: GeomPoint [constr] X=-18.8438 Y=10.16 Z=0
    g8: Circle [constr] CenterX=-31.5438 CenterY=10.16 CenterZ=0 NormalX=0 NormalY=0 NormalZ=1 AngleXU=0 Radius=0.4445
    g9: Circle CenterX=-29.0038 CenterY=10.16 CenterZ=0 NormalX=0 NormalY=0 NormalZ=1 AngleXU=0 Radius=0.4445
  constraints (23):
    c: DistanceX(g-3,g-1) = 37.8938
    c: Distance(g-3,g-4) = 22.86
    c: Coincident(g1,g2)
    c: Coincident(g2,g3)
    c: Coincident(g3,g0)
    c: Vertical(g0)
    c: Vertical(g2)
    c: Horizontal(g1)
    c: Horizontal(g3)
    c: DistanceX(g3,g3) = 25.4
    c: DistanceY(g2,g2) = 20.32
    c: Symmetric(g-3,g-4,g4)
    c: Symmetric(g0,g0,g5)
    c: Horizontal(g5,g4)
    c: Symmetric(g2,g0,g7)
    c: Symmetric(g-3,g-3,g6)
    c: Vertical(g7,g6)
    c: Coincident(g8,g0)
    c: Diameter(g8) = 0.889
    c: Coincident(g1,g0)
    c: Horizontal(g0,g9)
    c: DistanceX(g0,g9) = 2.54
    c: Equal(g8,g9)
FEATURE [PartDesign::Pad] Pad
  Direction = (0,-1,2e-16)
  Length = 9.906
  Length2 = 10
  Profile = -> Sketch
  ReferenceAxis = -> Sketch [N_Axis]
  Refine = true
  Suppressed = false
  Type = 0
FEATURE [PartDesign::Body] Body001  label="Body"
  AllowCompound = false
  Group = -> [Binder,Sketch,Pad]
  Origin = -> Origin005
  Tip = -> Pad
FEATURE [App::Part] Ft232H_2_assembly  label="Ft232H-2-assembly"
  Group = -> [Part__Feature014,Part__Feature015,Part__Feature016,Body001]
  Origin = -> Origin004
